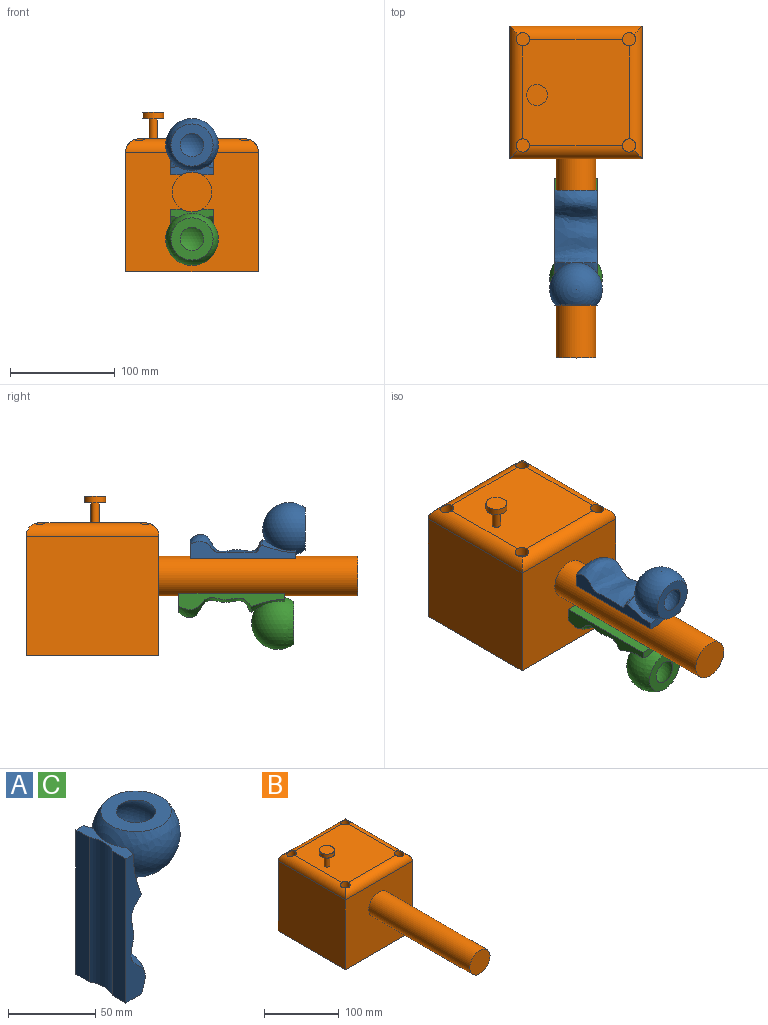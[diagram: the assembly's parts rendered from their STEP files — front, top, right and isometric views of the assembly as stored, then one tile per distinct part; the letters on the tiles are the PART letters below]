
ASSEMBLY  parts=3 mates=2
PART A: 12 faces, bbox 72.6x69.4x138.9 mm
  f0: plane 101.14x10.66mm, normal (-1,0,0), area 1077.9mm2, adj f4,f8,f9,f11
  f1: sphere r=18.92mm, area 4062.2mm2, adj f2
  f2: plane 40.32x40.32mm, normal (0,0,1), area 881.7mm2, adj f1,f3
  f3: sphere r=25.27mm, area 5373.9mm2, adj f2,f4,f7
  f4: plane 59.18x26.87mm, normal (0,0,1), area 206.6mm2, adj f0,f3,f5,f6,f7,f8,f11
  f5: plane 101.14x10.66mm, normal (-1,0,0), area 1077.9mm2, adj f4,f6,f9,f11
  f6: plane 111.39x26.61mm, normal (0,1,0), area 891.2mm2, adj f4,f5,f7,f9,f10
  f7: bspline ~40.32x31.75mm, area 608.8mm2, adj f3,f4,f6,f8,f10
  f8: plane 101.41x15.99mm, normal (0,-1,0), area 854.1mm2, adj f0,f4,f7,f9,f10
  f9: plane 40.33x18.45mm, normal (0,0,-1), area 636.6mm2, adj f0,f5,f6,f8,f10,f11
  f10: bspline ~69.39x40.32mm, area 3382.9mm2, adj f6,f7,f8,f9
  f11: cylinder r=19.05mm len=101.14mm, axis (0,0,1), area 2012.6mm2, adj f0,f4,f5,f9
PART B: 24 faces, bbox 127x317.5x152.4 mm
  f0: plane 127x114.3mm, normal (1,0,0), area 14516.1mm2, adj f1,f3,f5,f8
  f1: plane 127x114.3mm, normal (0,1,0), area 14516.1mm2, adj f0,f2,f5,f9
  f2: plane 127x114.3mm, normal (-1,0,0), area 14516.1mm2, adj f1,f3,f5,f11
  f3: plane 127x114.3mm, normal (0,-1,0), area 13376mm2, adj f0,f2,f5,f6,f10
  f4: plane 101.6x101.6mm, normal (0,0,1), area 10147.5mm2, adj f8,f9,f10,f11,f12,f14,f16,f18
  f5: plane 127x127mm, normal (0,0,-1), area 16129mm2, adj f0,f1,f2,f3
  f6: cylinder r=19.05mm len=190.5mm, axis (0,1,0), area 22801.8mm2, adj f3,f7
  f7: plane 38.1x38.1mm, normal (0,-1,0), area 1140.1mm2, adj f6
  f8: cylinder r=12.7mm len=127mm, axis (0,-1,0), area 2250.4mm2, adj f0,f4,f9,f10,f16,f18
  f9: cylinder r=12.7mm len=127mm, axis (1,0,0), area 2250.4mm2, adj f1,f4,f8,f11,f12,f18
  f10: cylinder r=12.7mm len=127mm, axis (-1,0,0), area 2250.4mm2, adj f3,f4,f8,f11,f14,f16
  f11: cylinder r=12.7mm len=127mm, axis (0,1,0), area 2250.4mm2, adj f2,f4,f9,f10,f12,f14
  f12: cylinder r=6.35mm len=12.7mm, axis (0,0,1), area 349.6mm2, adj f4,f9,f11,f13
  f13: plane 12.7x12.7mm, normal (0,0,1), area 126.7mm2, adj f12
  f14: cylinder r=6.35mm len=12.7mm, axis (0,0,1), area 349.6mm2, adj f4,f10,f11,f15
  f15: plane 12.7x12.7mm, normal (0,0,1), area 126.7mm2, adj f14
  f16: cylinder r=6.35mm len=12.7mm, axis (0,0,1), area 349.6mm2, adj f4,f8,f10,f17
  f17: plane 12.7x12.7mm, normal (0,0,1), area 126.7mm2, adj f16
  f18: cylinder r=6.35mm len=12.7mm, axis (0,0,1), area 349.6mm2, adj f4,f8,f9,f19
  f19: plane 12.7x12.7mm, normal (0,0,1), area 126.7mm2, adj f18
  f20: cylinder r=3.92mm len=19.05mm, axis (0,0,-1), area 469.7mm2, adj f4,f23
  f21: cylinder r=10.04mm len=20.08mm, axis (0,0,-1), area 400.6mm2, adj f22,f23
  f22: plane 20.08x20.08mm, normal (0,0,1), area 316.7mm2, adj f21
  f23: plane 20.08x20.08mm, normal (0,0,-1), area 268.3mm2, adj f20,f21
PART C: same geometry as A
PLACE A rot(axis=(0.58,-0.58,0.58),120deg) t=(-63.5,-251.69,102.24)mm
PLACE B t=(-63.5,-63.5,76.2)mm
PLACE C rot(axis=(0.58,0.58,-0.58),120deg) t=(-63.5,-240.98,50.16)mm
MATE slider C.f11 <-> B.f6  axis (0,-1,0) through (-63.5,-196.76,76.2)mm
MATE slider A.f11 <-> B.f6  axis (0,-1,0) through (-63.5,-207.48,76.2)mm
